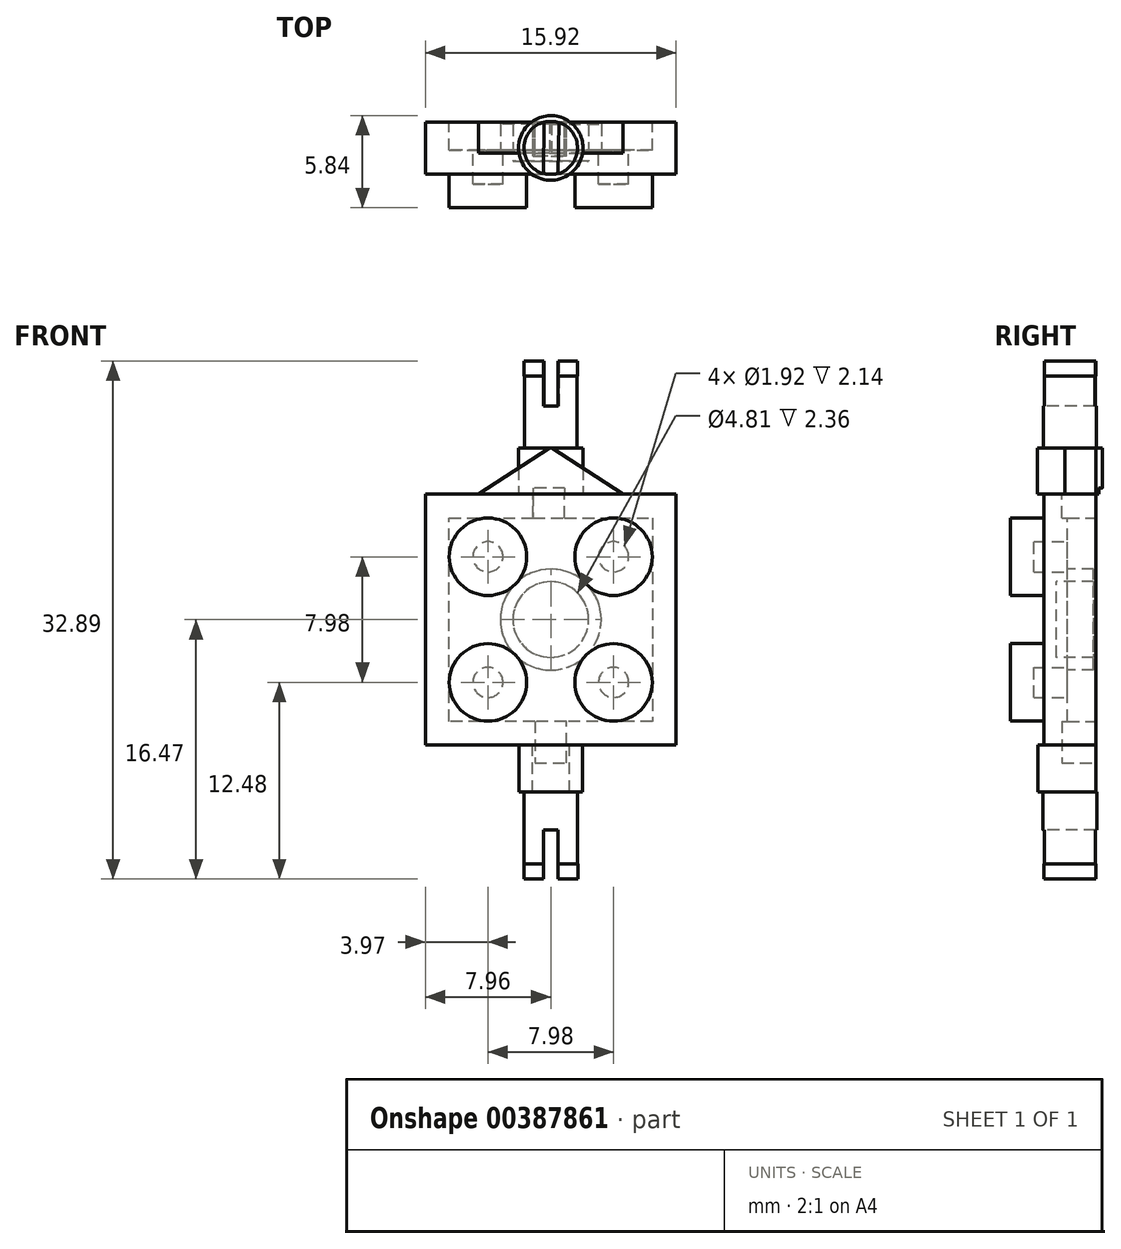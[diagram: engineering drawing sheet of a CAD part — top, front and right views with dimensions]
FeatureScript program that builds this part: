
annotation { "Feature Type Name" : "Feature", "Feature Type Description" : "" }
export const myFeature = defineFeature(function(context is Context, id is Id, definition is map)
    precondition{}
    {
        {
            var Q0;
            Q0=qCreatedBy(makeId("Front.planeOp"),FACE);
            var sketch = newSketch(context, id + "F0", { "sketchPlane" : qUnion([Q0])});
            skLineSegment(sketch, "E0", {"start": v(0, 0) * mm, "end": v(0, 15.92) * mm});
            skLineSegment(sketch, "E1", {"start": v(0, 15.92) * mm, "end": v(15.92, 15.92) * mm});
            skLineSegment(sketch, "E2", {"start": v(15.92, 15.92) * mm, "end": v(15.92, 0) * mm});
            skLineSegment(sketch, "E3", {"start": v(15.92, 0) * mm, "end": v(0, 0) * mm});
            skSolve(sketch);
        }
        {
            var Q0;
            Q0=makeQuery(id+"F0.imprint","IMPRINT",FACE,{"disambiguationData":[TD([[makeQuery(id+"F0.imprint","IMPRINT",EDGE,{"derivedFrom":sQuery(id+"F0.wireOp",EDGE,"E0")}),-1.0]])]});
            extrude(context, id + "F1", {"entities" : qUnion([Q0]), "depth" : 3.3 * mm});
        }
        {
            var Q0;
            Q0=makeQuery(id+"F1.opExtrude","CAP_FACE",FACE,{"disambiguationData":[OSD([sQuery(id+"F0.wireOp",EDGE,"E0"),sQuery(id+"F0.wireOp",EDGE,"E1"),sQuery(id+"F0.wireOp",EDGE,"E2"),sQuery(id+"F0.wireOp",EDGE,"E3")])],"isStart":false});
            var sketch = newSketch(context, id + "F2", { "sketchPlane" : qUnion([Q0])});
            skCircle(sketch, "E4", {"center": v(3.97, 11.95) * mm, "radius": 2.46 * mm});
            skCircle(sketch, "E5", {"center": v(11.95, 11.95) * mm, "radius": 2.46 * mm});
            skCircle(sketch, "E6", {"center": v(3.97, 3.97) * mm, "radius": 2.46 * mm});
            skCircle(sketch, "E7", {"center": v(11.95, 3.97) * mm, "radius": 2.46 * mm});
            skSolve(sketch);
        }
        {
            var Q0;
            Q0=qSketchRegion(id+"F2",true);
            extrude(context, id + "F3", {"entities" : qUnion([Q0]), "operationType" : NewBodyOperationType.ADD, "depth" : 2.14 * mm});
        }
        {
            var Q0;
            Q0=makeQuery(id+"F1.opExtrude","CAP_FACE",FACE,{"disambiguationData":[OSD([sQuery(id+"F0.wireOp",EDGE,"E0"),sQuery(id+"F0.wireOp",EDGE,"E1"),sQuery(id+"F0.wireOp",EDGE,"E2"),sQuery(id+"F0.wireOp",EDGE,"E3")])],"isStart":true});
            shell(context, id + "F4", {"entities" : qUnion([Q0]), "thickness" : 1.5 * mm});
        }
        {
            var Q0;
            Q0=makeQuery(id+"F4.opShell","OFFSET_FACE",FACE,{"disambiguationData":[OSD([sQuery(id+"F0.wireOp",EDGE,"E0"),sQuery(id+"F0.wireOp",EDGE,"E1"),sQuery(id+"F0.wireOp",EDGE,"E2"),sQuery(id+"F0.wireOp",EDGE,"E3")])]});
            var sketch = newSketch(context, id + "F5", { "sketchPlane" : qUnion([Q0])});
            skCircle(sketch, "E8", {"center": v(-7.96, 7.96) * mm, "radius": 3.2 * mm});
            skPoint(sketch, "E8.centerSnap0", {"position": v(-7.96, 14.42) * mm});
            skPoint(sketch, "E8.centerSnap1", {"position": v(-1.5, 7.96) * mm});
            skSolve(sketch);
        }
        {
            var Q0;
            Q0=makeQuery(id+"F5.imprint","IMPRINT",FACE,{"disambiguationData":[TD([[makeQuery(id+"F5.imprint","IMPRINT",EDGE,{"derivedFrom":sQuery(id+"F5.wireOp",EDGE,"E8")}),1.0]])]});
            extrude(context, id + "F6", {"entities" : qUnion([Q0]), "operationType" : NewBodyOperationType.ADD, "depth" : 1.66 * mm});
        }
        {
            var Q0;
            Q0=makeQuery(id+"F6.opExtrude","CAP_FACE",FACE,{"disambiguationData":[OSD([sQuery(id+"F5.wireOp",EDGE,"E8")])],"isStart":false});
            shell(context, id + "F7", {"entities" : qUnion([Q0]), "thickness" : .80 * mm});
        }
        {
            var Q0;
            Q0=makeQuery(id+"F1.opExtrude","SWEPT_FACE",FACE,{"disambiguationData":[OSD([sQuery(id+"F0.wireOp",EDGE,"E3")])]});
            var sketch = newSketch(context, id + "F8", { "sketchPlane" : qUnion([Q0])});
            skCircle(sketch, "E9", {"center": v(7.96, 1.65) * mm, "radius": 2.02 * mm});
            skPoint(sketch, "E9.centerSnap0", {"position": v(7.96, 3.3) * mm});
            skPoint(sketch, "E9.centerSnap1", {"position": v(0, 1.65) * mm});
            skSolve(sketch);
        }
        {
            var Q0;
            {var subQ0=sQuery(id+"F8.wireOp",EDGE,"E9");var subQ1=makeQuery(id+"F1.opExtrude","CAP_EDGE",EDGE,{"disambiguationData":[OSD([sQuery(id+"F0.wireOp",EDGE,"E3")])],"isStart":false});var subQ2=makeQuery(id+"F8.imprint","INTERSECT",VERTEX,{"disambiguationData":[OD(0.0)],"derivedFrom":[subQ1,subQ0]});Q0=makeQuery(id+"F8.imprint","IMPRINT",FACE,{"disambiguationData":[TD([[makeQuery(id+"F8.imprint","IMPRINT",EDGE,{"disambiguationData":[TD([[subQ2,1.0]])],"derivedFrom":subQ0}),1.0]])]});}
            var Q1;
            {var subQ0=sQuery(id+"F8.wireOp",EDGE,"E9");var subQ1=makeQuery(id+"F1.opExtrude","CAP_EDGE",EDGE,{"disambiguationData":[OSD([sQuery(id+"F0.wireOp",EDGE,"E3")])],"isStart":true});var subQ2=makeQuery(id+"F8.imprint","INTERSECT",VERTEX,{"disambiguationData":[OD(0.0)],"derivedFrom":[subQ1,subQ0]});Q1=makeQuery(id+"F8.imprint","IMPRINT",FACE,{"disambiguationData":[TD([[makeQuery(id+"F8.imprint","IMPRINT",EDGE,{"disambiguationData":[TD([[subQ2,-1.0]])],"derivedFrom":subQ0}),1.0]])]});}
            var Q2;
            {var subQ0=sQuery(id+"F8.wireOp",EDGE,"E9");var subQ1=sQuery(id+"F0.wireOp",EDGE,"E3");var subQ2=makeQuery(id+"F1.opExtrude","CAP_EDGE",EDGE,{"disambiguationData":[OSD([subQ1])],"isStart":false});var subQ3=makeQuery(id+"F8.imprint","INTERSECT",VERTEX,{"disambiguationData":[OD(0.0)],"derivedFrom":[subQ2,subQ0]});Q2=makeQuery(id+"F8.imprint","IMPRINT",FACE,{"disambiguationData":[TD([[makeQuery(id+"F8.imprint","IMPRINT",EDGE,{"disambiguationData":[TD([[subQ3,-1.0]])],"derivedFrom":subQ0}),1.0]])]});}
            extrude(context, id + "F9", {"entities" : qUnion([Q0, Q1, Q2]), "operationType" : NewBodyOperationType.ADD, "depth" : 8 * mm});
        }
        {
            var Q0;
            Q0=makeQuery(id+"F1.opExtrude","SWEPT_FACE",FACE,{"disambiguationData":[OSD([sQuery(id+"F0.wireOp",EDGE,"E1")])]});
            var sketch = newSketch(context, id + "F10", { "sketchPlane" : qUnion([Q0])});
            skCircle(sketch, "E10", {"center": v(7.96, -1.65) * mm, "radius": 2.05 * mm});
            skPoint(sketch, "E10.centerSnap0", {"position": v(7.96, -3.3) * mm});
            skPoint(sketch, "E10.centerSnap1", {"position": v(15.92, -1.65) * mm});
            skSolve(sketch);
        }
        {
            var Q0;
            {var subQ0=sQuery(id+"F10.wireOp",EDGE,"E10");var subQ1=makeQuery(id+"F1.opExtrude","CAP_EDGE",EDGE,{"disambiguationData":[OSD([sQuery(id+"F0.wireOp",EDGE,"E1")])],"isStart":true});var subQ2=makeQuery(id+"F10.imprint","INTERSECT",VERTEX,{"disambiguationData":[OD(0.0)],"derivedFrom":[subQ1,subQ0]});Q0=makeQuery(id+"F10.imprint","IMPRINT",FACE,{"disambiguationData":[TD([[makeQuery(id+"F10.imprint","IMPRINT",EDGE,{"disambiguationData":[TD([[subQ2,1.0]])],"derivedFrom":subQ0}),1.0]])]});}
            var Q1;
            {var subQ0=sQuery(id+"F10.wireOp",EDGE,"E10");var subQ1=makeQuery(id+"F1.opExtrude","CAP_EDGE",EDGE,{"disambiguationData":[OSD([sQuery(id+"F0.wireOp",EDGE,"E1")])],"isStart":false});var subQ2=makeQuery(id+"F10.imprint","INTERSECT",VERTEX,{"disambiguationData":[OD(0.0)],"derivedFrom":[subQ1,subQ0]});Q1=makeQuery(id+"F10.imprint","IMPRINT",FACE,{"disambiguationData":[TD([[makeQuery(id+"F10.imprint","IMPRINT",EDGE,{"disambiguationData":[TD([[subQ2,-1.0]])],"derivedFrom":subQ0}),1.0]])]});}
            var Q2;
            {var subQ0=sQuery(id+"F10.wireOp",EDGE,"E10");var subQ1=sQuery(id+"F0.wireOp",EDGE,"E1");var subQ2=makeQuery(id+"F1.opExtrude","CAP_EDGE",EDGE,{"disambiguationData":[OSD([subQ1])],"isStart":true});var subQ3=makeQuery(id+"F10.imprint","INTERSECT",VERTEX,{"disambiguationData":[OD(0.0)],"derivedFrom":[subQ2,subQ0]});Q2=makeQuery(id+"F10.imprint","IMPRINT",FACE,{"disambiguationData":[TD([[makeQuery(id+"F10.imprint","IMPRINT",EDGE,{"disambiguationData":[TD([[subQ3,-1.0]])],"derivedFrom":subQ0}),1.0]])]});}
            extrude(context, id + "F11", {"entities" : qUnion([Q0, Q1, Q2]), "operationType" : NewBodyOperationType.ADD, "depth" : 8 * mm});
        }
        {
            var Q0;
            Q0=makeQuery(id+"F1.opExtrude","CAP_FACE",FACE,{"disambiguationData":[OSD([sQuery(id+"F0.wireOp",EDGE,"E0"),sQuery(id+"F0.wireOp",EDGE,"E1"),sQuery(id+"F0.wireOp",EDGE,"E2"),sQuery(id+"F0.wireOp",EDGE,"E3")])],"isStart":true});
            var sketch = newSketch(context, id + "F12", { "sketchPlane" : qUnion([Q0])});
            skLineSegment(sketch, "E11", {"start": v(-3.4, 0) * mm, "end": v(-7.96, 0) * mm});
            skLineSegment(sketch, "E12", {"start": v(-7.96, 0) * mm, "end": v(-7.96, -3) * mm});
            skLineSegment(sketch, "E13", {"start": v(-7.96, -3) * mm, "end": v(-3.4, 0) * mm});
            skLineSegment(sketch, "E14", {"start": v(-7.96, 0) * mm, "end": v(-12.53, 0) * mm});
            skLineSegment(sketch, "E15", {"start": v(-12.53, 0) * mm, "end": v(-7.96, -3) * mm});
            skSolve(sketch);
        }
        {
            var Q0;
            {var subQ0=sQuery(id+"F12.wireOp",EDGE,"E12");Q0=makeQuery(id+"F12.imprint","IMPRINT",FACE,{"disambiguationData":[TD([[makeQuery(id+"F12.imprint","IMPRINT",EDGE,{"derivedFrom":subQ0}),-1.0]])]});}
            var Q1;
            {var subQ2=sQuery(id+"F12.wireOp",EDGE,"E12");Q1=makeQuery(id+"F12.imprint","IMPRINT",FACE,{"disambiguationData":[TD([[makeQuery(id+"F12.imprint","IMPRINT",EDGE,{"derivedFrom":subQ2}),1.0]])]});}
            var Q2;
            Q2 = qSketchRegion(id + "F14", true);
            extrude(context, id + "F13", {"entities" : qUnion([Q0, Q1, Q2]), "oppositeDirection" : true, "depth" : 1.95 * mm});
        }
        {
            var Q0;
            Q0=makeQuery(id+"F1.opExtrude","CAP_FACE",FACE,{"disambiguationData":[OSD([sQuery(id+"F0.wireOp",EDGE,"E0"),sQuery(id+"F0.wireOp",EDGE,"E1"),sQuery(id+"F0.wireOp",EDGE,"E2"),sQuery(id+"F0.wireOp",EDGE,"E3")])],"isStart":true});
            var sketch = newSketch(context, id + "F14", { "sketchPlane" : qUnion([Q0])});
            skLineSegment(sketch, "E16", {"start": v(-12.55, 15.92) * mm, "end": v(-7.96, 18.92) * mm});
            skLineSegment(sketch, "E17", {"start": v(-7.96, 18.92) * mm, "end": v(-7.96, 15.92) * mm});
            skLineSegment(sketch, "E18", {"start": v(-7.96, 15.92) * mm, "end": v(-12.55, 15.92) * mm});
            skLineSegment(sketch, "E19", {"start": v(-7.96, 18.92) * mm, "end": v(-3.37, 15.92) * mm});
            skLineSegment(sketch, "E20", {"start": v(-3.37, 15.92) * mm, "end": v(-7.96, 15.92) * mm});
            skSolve(sketch);
        }
        {
            var Q0;
            {var subQ0=sQuery(id+"F14.wireOp",EDGE,"E17");Q0=makeQuery(id+"F14.imprint","IMPRINT",FACE,{"disambiguationData":[TD([[makeQuery(id+"F14.imprint","IMPRINT",EDGE,{"derivedFrom":subQ0}),1.0]])]});}
            var Q1;
            {var subQ0=sQuery(id+"F14.wireOp",EDGE,"E16");Q1=makeQuery(id+"F14.imprint","IMPRINT",FACE,{"disambiguationData":[TD([[makeQuery(id+"F14.imprint","IMPRINT",EDGE,{"derivedFrom":subQ0}),-1.0]])]});}
            extrude(context, id + "F15", {"entities" : qUnion([Q0, Q1]), "oppositeDirection" : true, "depth" : 1.98 * mm});
        }
        {
            var Q0;
            Q0=makeQuery(id+"F11.opExtrude","CAP_FACE",FACE,{"disambiguationData":[OSD([sQuery(id+"F10.wireOp",EDGE,"E10")])],"isStart":false});
            var sketch = newSketch(context, id + "F16", { "sketchPlane" : qUnion([Q0])});
            skCircle(sketch, "E21", {"center": v(7.96, -1.65) * mm, "radius": 3 * mm});
            skSolve(sketch);
        }
        {
            var Q0;
            Q0=qSketchRegion(id+"F16",true);
            extrude(context, id + "F17", {"entities" : qUnion([Q0]), "operationType" : NewBodyOperationType.REMOVE, "oppositeDirection" : true, "depth" : 5.05 * mm});
        }
        {
            var Q0;
            Q0=makeQuery(id+"F17.boolean.opBoolean","COPY",FACE,{"derivedFrom":makeQuery(id+"F17.opExtrude","CAP_FACE",FACE,{"disambiguationData":[OSD([sQuery(id+"F16.wireOp",EDGE,"E21")])],"isStart":false})});
            var sketch = newSketch(context, id + "F18", { "sketchPlane" : qUnion([Q0])});
            skCircle(sketch, "E22", {"center": v(7.96, -1.65) * mm, "radius": 1.68 * mm});
            skSolve(sketch);
        }
        {
            var Q0;
            Q0=qSketchRegion(id+"F18",true);
            extrude(context, id + "F19", {"entities" : qUnion([Q0]), "depth" : 4.55 * mm});
        }
        {
            var Q0;
            Q0=makeQuery(id+"F19.opExtrude","CAP_FACE",FACE,{"disambiguationData":[OSD([sQuery(id+"F18.wireOp",EDGE,"E22")])],"isStart":false});
            var sketch = newSketch(context, id + "F20", { "sketchPlane" : qUnion([Q0])});
            skCircle(sketch, "E23", {"center": v(7.96, -1.65) * mm, "radius": 1.7 * mm});
            skSolve(sketch);
        }
        {
            var Q0;
            Q0=qSketchRegion(id+"F20",true);
            var Q1;
            Q1=qSketchRegion(id+"F22",true);
            var Q2;
            Q2=qSketchRegion(id+"F24",true);
            extrude(context, id + "F21", {"entities" : qUnion([Q0, Q1, Q2]), "operationType" : NewBodyOperationType.ADD, "depth" : .96 * mm});
        }
        {
            var Q0;
            Q0=makeQuery(id+"F21.opExtrude","CAP_FACE",FACE,{"disambiguationData":[OSD([sQuery(id+"F20.wireOp",EDGE,"E23")])],"isStart":false});
            var sketch = newSketch(context, id + "F22", { "sketchPlane" : qUnion([Q0])});
            skLineSegment(sketch, "E24", {"start": v(8.5, 0.64) * mm, "end": v(7.55, 0.64) * mm});
            skLineSegment(sketch, "E25", {"start": v(8.43, -3.28) * mm, "end": v(8.5, 0.64) * mm});
            skLineSegment(sketch, "E26", {"start": v(7.55, 0.64) * mm, "end": v(7.49, -3.28) * mm});
            skArc(sketch, "E27", {"start": v(7.49, -3.28) * mm, "mid": v(7.96, -3.35) * mm, "end": v(8.43, -3.28) * mm});
            skSolve(sketch);
        }
        {
            var Q0;
            Q0=qSketchRegion(id+"F22",true);
            extrude(context, id + "F23", {"entities" : qUnion([Q0]), "operationType" : NewBodyOperationType.REMOVE, "oppositeDirection" : true, "depth" : 2.86 * mm});
        }
        {
            var Q0;
            Q0=makeQuery(id+"F9.opExtrude","CAP_FACE",FACE,{"disambiguationData":[OSD([sQuery(id+"F8.wireOp",EDGE,"E9")])],"isStart":false});
            var sketch = newSketch(context, id + "F24", { "sketchPlane" : qUnion([Q0])});
            skCircle(sketch, "E28", {"center": v(7.96, 1.65) * mm, "radius": 2.04 * mm});
            skSolve(sketch);
        }
        {
            var Q0;
            Q0=qSketchRegion(id+"F24",true);
            extrude(context, id + "F25", {"entities" : qUnion([Q0]), "operationType" : NewBodyOperationType.REMOVE, "oppositeDirection" : true, "depth" : 5 * mm});
        }
        {
            var Q0;
            Q0=makeQuery(id+"F25.boolean.opBoolean","COPY",FACE,{"derivedFrom":makeQuery(id+"F25.opExtrude","CAP_FACE",FACE,{"disambiguationData":[OSD([sQuery(id+"F24.wireOp",EDGE,"E28")])],"isStart":false})});
            var sketch = newSketch(context, id + "F26", { "sketchPlane" : qUnion([Q0])});
            skCircle(sketch, "E29", {"center": v(7.96, 1.65) * mm, "radius": 1.7 * mm});
            skSolve(sketch);
        }
        {
            var Q0;
            Q0=qSketchRegion(id+"F26",true);
            extrude(context, id + "F27", {"entities" : qUnion([Q0]), "operationType" : NewBodyOperationType.ADD, "depth" : 4.55 * mm});
        }
        {
            var Q0;
            Q0=makeQuery(id+"F27.opExtrude","CAP_FACE",FACE,{"disambiguationData":[OSD([sQuery(id+"F26.wireOp",EDGE,"E29")])],"isStart":false});
            var sketch = newSketch(context, id + "F28", { "sketchPlane" : qUnion([Q0])});
            skCircle(sketch, "E30", {"center": v(7.96, 1.65) * mm, "radius": 1.72 * mm});
            skSolve(sketch);
        }
        {
            var Q0;
            Q0=qSketchRegion(id+"F28",true);
            extrude(context, id + "F29", {"entities" : qUnion([Q0]), "operationType" : NewBodyOperationType.ADD, "depth" : .96 * mm});
        }
        {
            var Q0;
            Q0=makeQuery(id+"F29.opExtrude","CAP_FACE",FACE,{"disambiguationData":[OSD([sQuery(id+"F28.wireOp",EDGE,"E30")])],"isStart":false});
            var sketch = newSketch(context, id + "F30", { "sketchPlane" : qUnion([Q0])});
            skLineSegment(sketch, "E31", {"start": v(8.43, -0.27) * mm, "end": v(8.43, 3.68) * mm});
            skLineSegment(sketch, "E32", {"start": v(8.43, 3.68) * mm, "end": v(7.5, 3.68) * mm});
            skLineSegment(sketch, "E33", {"start": v(7.5, 3.68) * mm, "end": v(7.5, -0.27) * mm});
            skLineSegment(sketch, "E34", {"start": v(7.5, -0.27) * mm, "end": v(8.43, -0.27) * mm});
            skSolve(sketch);
        }
        {
            var Q0;
            Q0=qSketchRegion(id+"F30",true);
            var Q1;
            Q1 = qSketchRegion(id + "F32", true);
            extrude(context, id + "F31", {"entities" : qUnion([Q0, Q1]), "operationType" : NewBodyOperationType.REMOVE, "oppositeDirection" : true, "depth" : 3.1 * mm});
        }
        {
            var Q0;
            Q0=makeQuery(id+"F1.opExtrude","CAP_FACE",FACE,{"disambiguationData":[OSD([sQuery(id+"F0.wireOp",EDGE,"E0"),sQuery(id+"F0.wireOp",EDGE,"E1"),sQuery(id+"F0.wireOp",EDGE,"E2"),sQuery(id+"F0.wireOp",EDGE,"E3")])],"isStart":true});
            var sketch = newSketch(context, id + "F32", { "sketchPlane" : qUnion([Q0])});
            skLineSegment(sketch, "E35", {"start": v(-8.83, 14.42) * mm, "end": v(-8.83, 17.06) * mm});
            skLineSegment(sketch, "E36", {"start": v(-8.83, 17.06) * mm, "end": v(-6.83, 17.06) * mm});
            skLineSegment(sketch, "E37", {"start": v(-6.83, 17.06) * mm, "end": v(-6.83, 14.42) * mm});
            skLineSegment(sketch, "E38", {"start": v(-6.83, 14.42) * mm, "end": v(-8.83, 14.42) * mm});
            skSolve(sketch);
        }
        {
            var Q0;
            {var subQ0=sQuery(id+"F32.wireOp",EDGE,"E38");Q0=makeQuery(id+"F32.imprint","IMPRINT",FACE,{"disambiguationData":[TD([[makeQuery(id+"F32.imprint","IMPRINT",EDGE,{"derivedFrom":subQ0}),-1.0]])]});}
            extrude(context, id + "F33", {"entities" : qUnion([Q0]), "operationType" : NewBodyOperationType.REMOVE, "oppositeDirection" : true, "depth" : 2.16 * mm});
        }
        {
            var Q0;
            Q0=makeQuery(id+"F15.opExtrude","CAP_FACE",FACE,{"disambiguationData":[OSD([sQuery(id+"F14.wireOp",EDGE,"E16"),sQuery(id+"F14.wireOp",EDGE,"E18"),sQuery(id+"F14.wireOp",EDGE,"E19"),sQuery(id+"F14.wireOp",EDGE,"E20")])],"isStart":true});
            var sketch = newSketch(context, id + "F34", { "sketchPlane" : qUnion([Q0])});
            skLineSegment(sketch, "E39", {"start": v(-8.84, 15.8) * mm, "end": v(-8.84, 16.31) * mm});
            skLineSegment(sketch, "E40", {"start": v(-8.84, 15.8) * mm, "end": v(-6.82, 15.8) * mm});
            skLineSegment(sketch, "E41", {"start": v(-8.84, 16.31) * mm, "end": v(-6.82, 16.31) * mm});
            skLineSegment(sketch, "E42", {"start": v(-6.82, 16.31) * mm, "end": v(-6.82, 15.8) * mm});
            skSolve(sketch);
        }
        {
            var Q0;
            Q0=qSketchRegion(id+"F34",true);
            extrude(context, id + "F35", {"entities" : qUnion([Q0]), "operationType" : NewBodyOperationType.REMOVE, "depth" : 2.16 * mm});
        }
        {
            var Q0;
            Q0=makeQuery(id+"F1.opExtrude","CAP_FACE",FACE,{"disambiguationData":[OSD([sQuery(id+"F0.wireOp",EDGE,"E0"),sQuery(id+"F0.wireOp",EDGE,"E1"),sQuery(id+"F0.wireOp",EDGE,"E2"),sQuery(id+"F0.wireOp",EDGE,"E3")])],"isStart":true});
            var sketch = newSketch(context, id + "F36", { "sketchPlane" : qUnion([Q0])});
            skLineSegment(sketch, "E43", {"start": v(-6.95, 1.5) * mm, "end": v(-6.95, -1.14) * mm});
            skLineSegment(sketch, "E44", {"start": v(-6.95, -1.14) * mm, "end": v(-8.95, -1.14) * mm});
            skLineSegment(sketch, "E45", {"start": v(-8.95, -1.14) * mm, "end": v(-8.95, 1.5) * mm});
            skLineSegment(sketch, "E46", {"start": v(-8.95, 1.5) * mm, "end": v(-6.95, 1.5) * mm});
            skSolve(sketch);
        }
        {
            var Q0;
            Q0=qSketchRegion(id+"F36",true);
            extrude(context, id + "F37", {"entities" : qUnion([Q0]), "operationType" : NewBodyOperationType.REMOVE, "oppositeDirection" : true, "depth" : 2.16 * mm});
        }
    });
